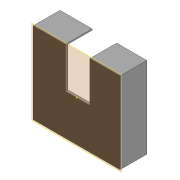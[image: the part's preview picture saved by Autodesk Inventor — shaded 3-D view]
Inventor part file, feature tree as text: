
AUTODESK INVENTOR PART (.ipt)
format: ipt  version: 2018.1 (Build 221171000, 171)  size: 114,688 bytes
history: native  units: in
note: dims shown in document units (in); Inventor stores cm internally (conversion verified against a paired STEP export)
features: sketch x6, extrude x5, plane x1
ambient origin geometry x8: Origin, YZ Plane, XZ Plane, XY Plane, X Axis, Y Axis, Z Axis, Center Point
bodies: Solid1 (feature_tree)
feature tree (12):
  plane  "Work Plane1"
  extrude  "Extrusion1"  Depth=3.25in
  extrude  "Extrusion2"  Depth=3.35in
  extrude  "Extrusion3"  Depth=0.1in TaperAngle=0.0deg
  extrude  "Extrusion4"  Depth=0.1in TaperAngle=0.0deg
  extrude  "Extrusion5"  [1 undecoded]
  sketch  "Sketch8"
  sketch  "Sketch1"  dims[d1=3.475in d2=3.25in]
  sketch  "Sketch2"  dims[d3=3.575in d4=3.35in]
  sketch  "Sketch5"  dims[d5=1.1in d6=0.0in d7=0.1in d8=0.0in]
  sketch  "Sketch6"  dims[d9=0.1in d10=0.0in d11=0.1in d12=0.0in]
  sketch  "Sketch7"  dims[d13=0.1in d14=0.0in]
note: 1 required parameter value undecoded (feature->parameter linkage not recoverable at this tier; creation-order binding heuristic only, values carry confidence <= 0.55)
